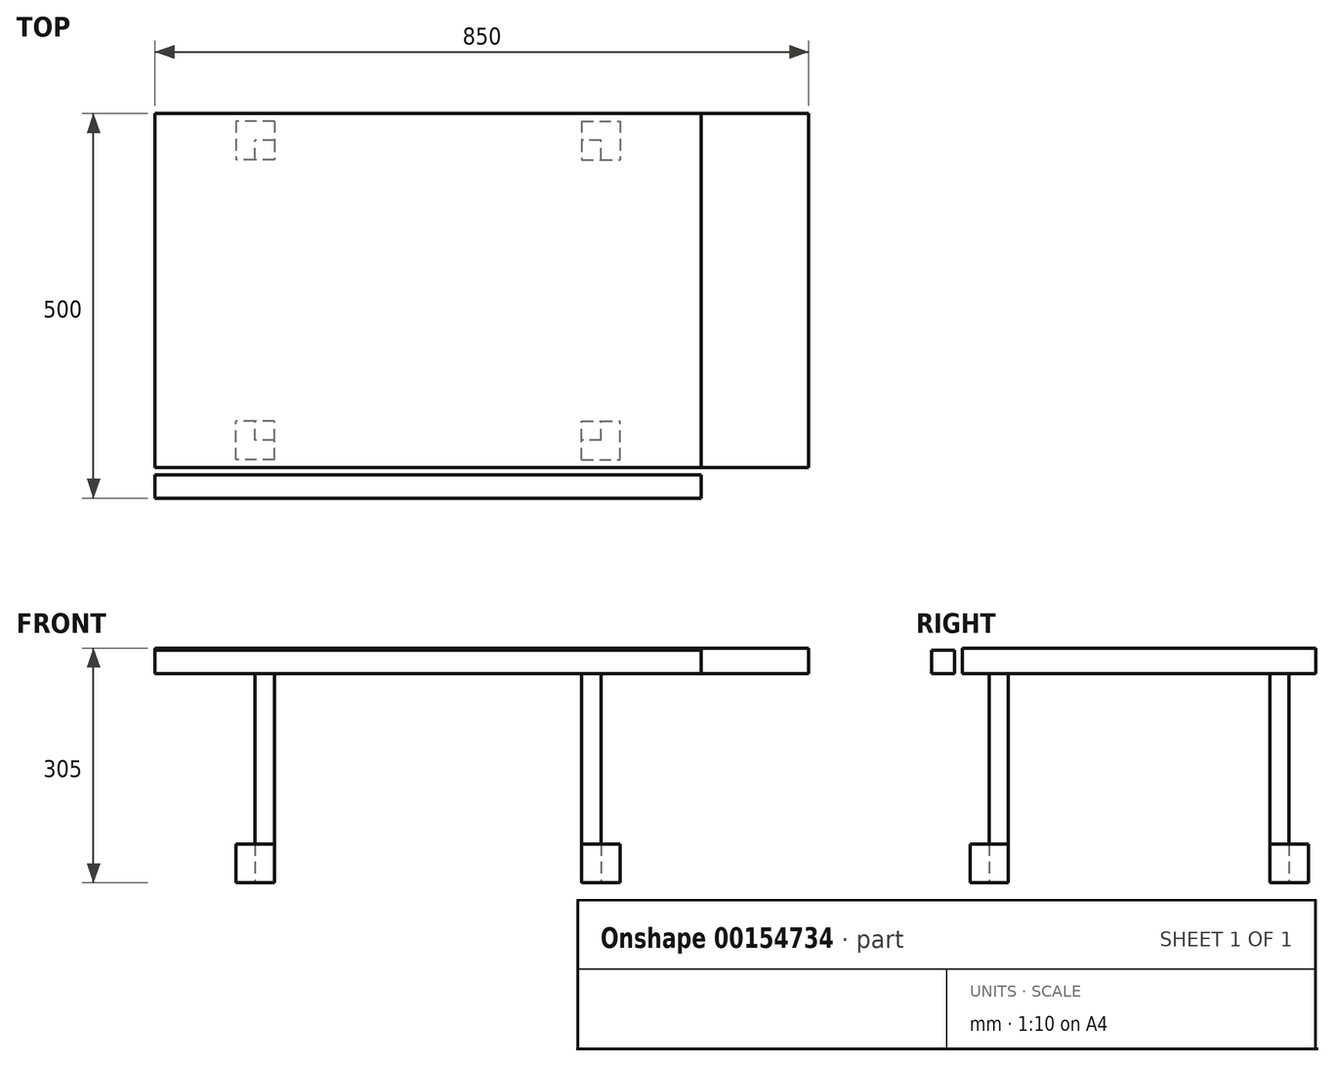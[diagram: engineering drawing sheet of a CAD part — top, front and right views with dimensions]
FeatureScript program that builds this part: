
annotation { "Feature Type Name" : "Feature", "Feature Type Description" : "" }
export const myFeature = defineFeature(function(context is Context, id is Id, definition is map)
    precondition{}
    {
        {
            var Q0;
            Q0=qCreatedBy(makeId("Top.planeOp"),FACE);
            var sketch = newSketch(context, id + "F0", { "sketchPlane" : qUnion([Q0])});
            skLineSegment(sketch, "E0.bottom", {"start": v(225, -195) * mm, "end": v(-225, -195) * mm});
            skLineSegment(sketch, "E0.top", {"start": v(225, 195) * mm, "end": v(-225, 195) * mm});
            skLineSegment(sketch, "E0.left", {"start": v(225, -195) * mm, "end": v(225, 195) * mm});
            skLineSegment(sketch, "E0.right", {"start": v(-225, -195) * mm, "end": v(-225, 195) * mm});
            skPoint(sketch, "E0.middle", {"position": v(0, 0) * mm});
            skLineSegment(sketch, "E1.bottom", {"start": v(25, -100) * mm, "end": v(-25, -100) * mm});
            skLineSegment(sketch, "E1.top", {"start": v(25, 100) * mm, "end": v(-25, 100) * mm});
            skLineSegment(sketch, "E1.left", {"start": v(25, -100) * mm, "end": v(25, 100) * mm});
            skLineSegment(sketch, "E1.right", {"start": v(-25, -100) * mm, "end": v(-25, 100) * mm});
            skLineSegment(sketch, "E2.bottom", {"start": v(-200, -220) * mm, "end": v(-250, -220) * mm});
            skLineSegment(sketch, "E2.top", {"start": v(-200, -170) * mm, "end": v(-250, -170) * mm});
            skLineSegment(sketch, "E2.left", {"start": v(-200, -220) * mm, "end": v(-200, -170) * mm});
            skLineSegment(sketch, "E2.right", {"start": v(-250, -220) * mm, "end": v(-250, -170) * mm});
            skPoint(sketch, "E2.middle", {"position": v(-225, -195) * mm});
            skLineSegment(sketch, "E3.MirrorCS", {"start": v(-250, 220) * mm, "end": v(-250, 170) * mm});
            skLineSegment(sketch, "E4.MirrorCS", {"start": v(-200, 220) * mm, "end": v(-250, 220) * mm});
            skLineSegment(sketch, "E5.MirrorCS", {"start": v(-200, 170) * mm, "end": v(-250, 170) * mm});
            skLineSegment(sketch, "E6.MirrorCS", {"start": v(-200, 220) * mm, "end": v(-200, 170) * mm});
            skLineSegment(sketch, "E7.MirrorCS", {"start": v(250, 220) * mm, "end": v(250, 170) * mm});
            skLineSegment(sketch, "E8.MirrorCS", {"start": v(250, -220) * mm, "end": v(250, -170) * mm});
            skLineSegment(sketch, "E9.MirrorCS", {"start": v(200, -220) * mm, "end": v(200, -170) * mm});
            skLineSegment(sketch, "E10.MirrorCS", {"start": v(200, 220) * mm, "end": v(200, 170) * mm});
            skLineSegment(sketch, "E11.MirrorCS", {"start": v(200, -220) * mm, "end": v(250, -220) * mm});
            skLineSegment(sketch, "E12.MirrorCS", {"start": v(200, -170) * mm, "end": v(250, -170) * mm});
            skLineSegment(sketch, "E13.MirrorCS", {"start": v(200, 170) * mm, "end": v(250, 170) * mm});
            skLineSegment(sketch, "E14.MirrorCS", {"start": v(200, 220) * mm, "end": v(250, 220) * mm});
            skLineSegment(sketch, "E15.bottom", {"start": v(355, -230) * mm, "end": v(-355, -230) * mm});
            skLineSegment(sketch, "E15.top", {"start": v(355, 230) * mm, "end": v(-355, 230) * mm});
            skLineSegment(sketch, "E15.left", {"start": v(355, -230) * mm, "end": v(355, 230) * mm});
            skLineSegment(sketch, "E15.right", {"start": v(-355, -230) * mm, "end": v(-355, 230) * mm});
            skLineSegment(sketch, "E16.bottom", {"start": v(-355, -230) * mm, "end": v(355, -230) * mm});
            skLineSegment(sketch, "E16.top", {"start": v(-355, -270) * mm, "end": v(355, -270) * mm});
            skLineSegment(sketch, "E16.left", {"start": v(-355, -230) * mm, "end": v(-355, -270) * mm});
            skLineSegment(sketch, "E16.right", {"start": v(355, -230) * mm, "end": v(355, -270) * mm});
            skLineSegment(sketch, "E17", {"start": v(-355, -240) * mm, "end": v(355, -240) * mm});
            skLineSegment(sketch, "E18.bottom", {"start": v(355, 230) * mm, "end": v(495, 230) * mm});
            skLineSegment(sketch, "E18.top", {"start": v(355, -230) * mm, "end": v(495, -230) * mm});
            skLineSegment(sketch, "E18.left", {"start": v(355, 230) * mm, "end": v(355, -230) * mm});
            skLineSegment(sketch, "E18.right", {"start": v(495, 230) * mm, "end": v(495, -230) * mm});
            skLineSegment(sketch, "E19.bottom", {"start": v(355, -230) * mm, "end": v(355, -230) * mm});
            skLineSegment(sketch, "E19.top", {"start": v(355, -230) * mm, "end": v(355, -230) * mm});
            skLineSegment(sketch, "E19.left", {"start": v(355, -230) * mm, "end": v(355, -230) * mm});
            skLineSegment(sketch, "E19.right", {"start": v(355, -230) * mm, "end": v(355, -230) * mm});
            skSolve(sketch);
        }
        {
            var Q0;
            Q0=makeQuery(id+"F0.imprint","IMPRINT",FACE,{"disambiguationData":[TD([[makeQuery(id+"F0.imprint","IMPRINT",EDGE,{"derivedFrom":sQuery(id+"F0.wireOp",EDGE,"E1.bottom")}),1.0]])]});
            var Q1;
            {var subQ0=sQuery(id+"F0.wireOp",EDGE,"E0.right");var subQ1=sQuery(id+"F0.wireOp",EDGE,"E0.top");var subQ2=makeQuery(id+"F0.imprint","INTERSECT",VERTEX,{"derivedFrom":[subQ1,subQ0]});Q1=makeQuery(id+"F0.imprint","IMPRINT",FACE,{"disambiguationData":[TD([[makeQuery(id+"F0.imprint","IMPRINT",EDGE,{"disambiguationData":[TD([[subQ2,1.0]])],"derivedFrom":subQ1}),1.0]])]});}
            var Q2;
            {var subQ0=sQuery(id+"F0.wireOp",EDGE,"E0.right");var subQ1=sQuery(id+"F0.wireOp",EDGE,"E0.bottom");var subQ2=makeQuery(id+"F0.imprint","INTERSECT",VERTEX,{"derivedFrom":[subQ1,subQ0]});Q2=makeQuery(id+"F0.imprint","IMPRINT",FACE,{"disambiguationData":[TD([[makeQuery(id+"F0.imprint","IMPRINT",EDGE,{"disambiguationData":[TD([[subQ2,1.0]])],"derivedFrom":subQ1}),-1.0]])]});}
            var Q3;
            {var subQ0=sQuery(id+"F0.wireOp",EDGE,"E0.left");var subQ1=sQuery(id+"F0.wireOp",EDGE,"E0.bottom");var subQ2=makeQuery(id+"F0.imprint","INTERSECT",VERTEX,{"derivedFrom":[subQ1,subQ0]});Q3=makeQuery(id+"F0.imprint","IMPRINT",FACE,{"disambiguationData":[TD([[makeQuery(id+"F0.imprint","IMPRINT",EDGE,{"disambiguationData":[TD([[subQ2,-1.0]])],"derivedFrom":subQ1}),-1.0]])]});}
            var Q4;
            {var subQ0=sQuery(id+"F0.wireOp",EDGE,"E0.left");var subQ1=sQuery(id+"F0.wireOp",EDGE,"E0.top");var subQ2=makeQuery(id+"F0.imprint","INTERSECT",VERTEX,{"derivedFrom":[subQ1,subQ0]});Q4=makeQuery(id+"F0.imprint","IMPRINT",FACE,{"disambiguationData":[TD([[makeQuery(id+"F0.imprint","IMPRINT",EDGE,{"disambiguationData":[TD([[subQ2,-1.0]])],"derivedFrom":subQ1}),1.0]])]});}
            extrude(context, id + "F1", {"entities" : qUnion([Q0, Q1, Q2, Q3, Q4]), "depth" : 272 * mm});
        }
        {
            var Q0;
            {var subQ1=sQuery(id+"F0.wireOp",EDGE,"E3.MirrorCS");Q0=makeQuery(id+"F0.imprint","IMPRINT",FACE,{"disambiguationData":[TD([[makeQuery(id+"F0.imprint","IMPRINT",EDGE,{"derivedFrom":subQ1}),1.0]])]});}
            var Q1;
            {var subQ8=sQuery(id+"F0.wireOp",EDGE,"E2.bottom");Q1=makeQuery(id+"F0.imprint","IMPRINT",FACE,{"disambiguationData":[TD([[makeQuery(id+"F0.imprint","IMPRINT",EDGE,{"derivedFrom":subQ8}),-1.0]])]});}
            var Q2;
            {var subQ4=sQuery(id+"F0.wireOp",EDGE,"E8.MirrorCS");Q2=makeQuery(id+"F0.imprint","IMPRINT",FACE,{"disambiguationData":[TD([[makeQuery(id+"F0.imprint","IMPRINT",EDGE,{"derivedFrom":subQ4}),1.0]])]});}
            var Q3;
            {var subQ0=sQuery(id+"F0.wireOp",EDGE,"E7.MirrorCS");Q3=makeQuery(id+"F0.imprint","IMPRINT",FACE,{"disambiguationData":[TD([[makeQuery(id+"F0.imprint","IMPRINT",EDGE,{"derivedFrom":subQ0}),-1.0]])]});}
            extrude(context, id + "F2", {"entities" : qUnion([Q0, Q1, Q2, Q3]), "depth" : 50 * mm});
        }
        {
            var Q0;
            Q0=makeQuery(id+"F1.opExtrude","CAP_FACE",FACE,{"disambiguationData":[OSD([sQuery(id+"F0.wireOp",EDGE,"E0.bottom"),sQuery(id+"F0.wireOp",EDGE,"E0.top"),sQuery(id+"F0.wireOp",EDGE,"E0.left"),sQuery(id+"F0.wireOp",EDGE,"E0.right"),sQuery(id+"F0.wireOp",EDGE,"E1.bottom"),sQuery(id+"F0.wireOp",EDGE,"E1.top"),sQuery(id+"F0.wireOp",EDGE,"E1.left"),sQuery(id+"F0.wireOp",EDGE,"E1.right")])],"isStart":false});
            var sketch = newSketch(context, id + "F3", { "sketchPlane" : qUnion([Q0])});
            skLineSegment(sketch, "E20.0.0", {"start": v(355, -230) * mm, "end": v(355, 230) * mm});
            skLineSegment(sketch, "E20.0.1", {"start": v(355, 230) * mm, "end": v(-355, 230) * mm});
            skLineSegment(sketch, "E20.0.2", {"start": v(-355, 230) * mm, "end": v(-355, -230) * mm});
            skLineSegment(sketch, "E20.0.3", {"start": v(-355, -230) * mm, "end": v(355, -230) * mm});
            skLineSegment(sketch, "E21.0.0", {"start": v(-355, -240) * mm, "end": v(-355, -270) * mm});
            skLineSegment(sketch, "E21.0.1", {"start": v(-355, -270) * mm, "end": v(355, -270) * mm});
            skLineSegment(sketch, "E21.0.2", {"start": v(355, -270) * mm, "end": v(355, -240) * mm});
            skLineSegment(sketch, "E21.0.3", {"start": v(355, -240) * mm, "end": v(-355, -240) * mm});
            skLineSegment(sketch, "E22.0.0", {"start": v(495, 230) * mm, "end": v(355, 230) * mm});
            skLineSegment(sketch, "E22.0.1", {"start": v(355, 230) * mm, "end": v(355, -230) * mm});
            skLineSegment(sketch, "E22.0.2", {"start": v(355, -230) * mm, "end": v(495, -230) * mm});
            skLineSegment(sketch, "E22.0.3", {"start": v(495, -230) * mm, "end": v(495, 230) * mm});
            skSolve(sketch);
        }
        {
            var Q0;
            Q0=makeQuery(id+"F3.imprint","IMPRINT",FACE,{"disambiguationData":[TD([[makeQuery(id+"F3.imprint","IMPRINT",EDGE,{"derivedFrom":sQuery(id+"F3.wireOp",EDGE,"E20.0.1")}),1.0]])]});
            var Q1;
            Q1=makeQuery(id+"F3.imprint","IMPRINT",FACE,{"disambiguationData":[TD([[makeQuery(id+"F3.imprint","IMPRINT",EDGE,{"derivedFrom":makeQuery(id+"F1.opExtrude","CAP_EDGE",EDGE,{"disambiguationData":[OSD([sQuery(id+"F0.wireOp",EDGE,"E0.bottom")])],"isStart":false})}),-1.0]])]});
            extrude(context, id + "F4", {"entities" : qUnion([Q0, Q1]), "flatOperationType" : FlatOperationType.REMOVE, "thickness1" : 5 * mm, "thickness2" : 0 * mm, "thickness" : 5 * mm, "offsetDistance" : 25 * mm, "startOffsetBound" : StartOffsetType.BLIND, "startOffsetDistance" : 25 * mm, "depth" : 33 * mm, "domain" : OperationDomain.MODEL});
        }
        {
            var Q0;
            Q0=makeQuery(id+"F3.imprint","IMPRINT",FACE,{"disambiguationData":[TD([[makeQuery(id+"F3.imprint","IMPRINT",EDGE,{"derivedFrom":sQuery(id+"F3.wireOp",EDGE,"E21.0.0")}),1.0]])]});
            extrude(context, id + "F5", {"entities" : qUnion([Q0]), "depth" : 30 * mm});
        }
        {
            var Q0;
            Q0=makeQuery(id+"F3.imprint","IMPRINT",FACE,{"disambiguationData":[TD([[makeQuery(id+"F3.imprint","IMPRINT",EDGE,{"derivedFrom":sQuery(id+"F3.wireOp",EDGE,"E22.0.0")}),1.0]])]});
            extrude(context, id + "F6", {"entities" : qUnion([Q0]), "depth" : 33 * mm});
        }
    });
